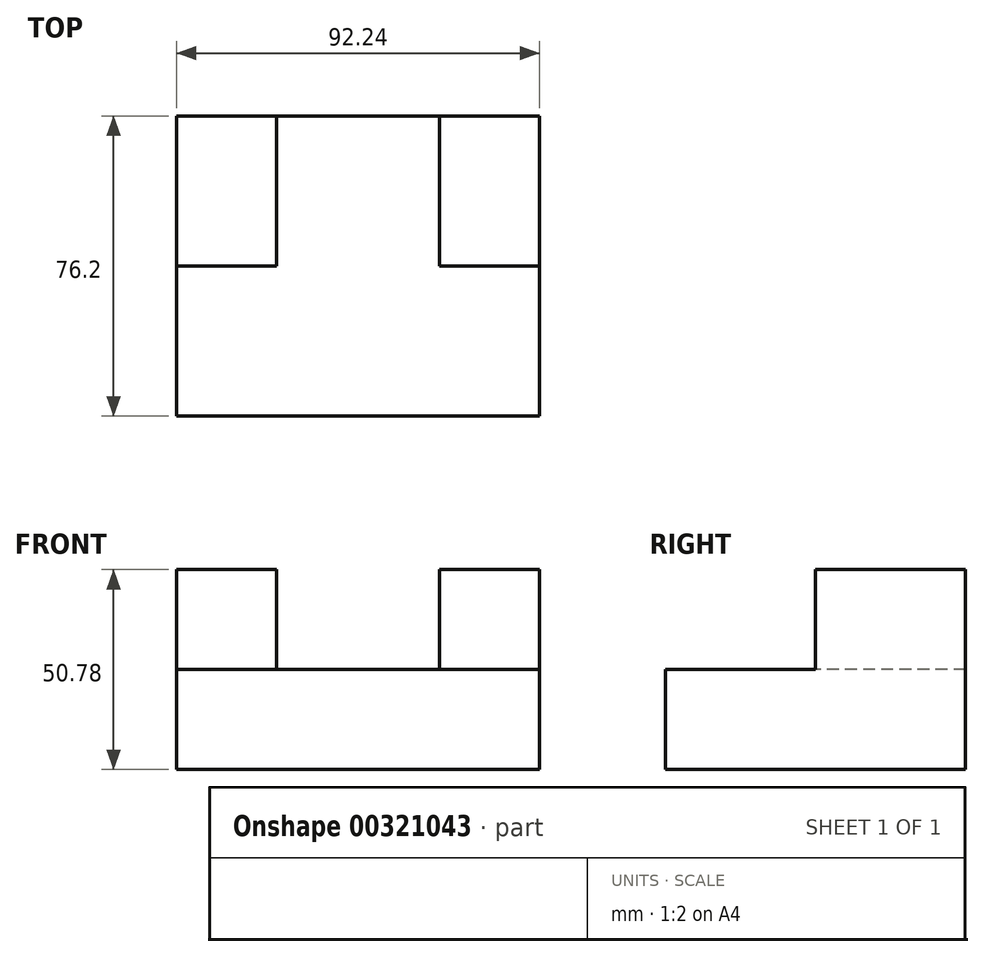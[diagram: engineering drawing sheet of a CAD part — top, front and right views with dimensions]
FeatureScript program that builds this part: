
annotation { "Feature Type Name" : "Feature", "Feature Type Description" : "" }
export const myFeature = defineFeature(function(context is Context, id is Id, definition is map)
    precondition{}
    {
        {
            var Q0;
            Q0=qCreatedBy(makeId("Front.planeOp"),FACE);
            var sketch = newSketch(context, id + "F0", { "sketchPlane" : qUnion([Q0])});
            skLineSegment(sketch, "E0", {"start": v(-58.8, -31.1) * mm, "end": v(33.43, -31.1) * mm});
            skLineSegment(sketch, "E1", {"start": v(33.43, -31.1) * mm, "end": v(33.43, -5.73) * mm});
            skLineSegment(sketch, "E2", {"start": v(33.43, -5.73) * mm, "end": v(-58.8, -5.73) * mm});
            skLineSegment(sketch, "E3", {"start": v(-58.8, -5.73) * mm, "end": v(-58.8, -31.1) * mm});
            skSolve(sketch);
        }
        {
            var Q0;
            Q0=makeQuery(id+"F0.imprint","IMPRINT",FACE,{"disambiguationData":[TD([[makeQuery(id+"F0.imprint","IMPRINT",EDGE,{"derivedFrom":sQuery(id+"F0.wireOp",EDGE,"E0")}),1.0]])]});
            extrude(context, id + "F1", {"entities" : qUnion([Q0]), "depth" : 76.2 * mm});
        }
        {
            var Q0;
            Q0=makeQuery(id+"F1.opExtrude","SWEPT_FACE",FACE,{"disambiguationData":[OSD([sQuery(id+"F0.wireOp",EDGE,"E2")])]});
            var sketch = newSketch(context, id + "F2", { "sketchPlane" : qUnion([Q0])});
            skLineSegment(sketch, "E4", {"start": v(-33.4, 0) * mm, "end": v(-33.4, -38.1) * mm});
            skLineSegment(sketch, "E5", {"start": v(-33.4, -38.1) * mm, "end": v(-58.8, -38.1) * mm});
            skLineSegment(sketch, "E6", {"start": v(-58.8, -38.1) * mm, "end": v(-58.8, 0) * mm});
            skLineSegment(sketch, "E7", {"start": v(-58.8, 0) * mm, "end": v(-33.4, 0) * mm});
            skSolve(sketch);
        }
        {
            var Q0;
            Q0=makeQuery(id+"F2.imprint","IMPRINT",FACE,{"disambiguationData":[TD([[makeQuery(id+"F2.imprint","IMPRINT",EDGE,{"derivedFrom":sQuery(id+"F2.wireOp",EDGE,"E4")}),-1.0]])]});
            extrude(context, id + "F3", {"entities" : qUnion([Q0]), "operationType" : NewBodyOperationType.ADD, "depth" : 25.4 * mm});
        }
        {
            var Q0;
            Q0=makeQuery(id+"F1.opExtrude","SWEPT_FACE",FACE,{"disambiguationData":[OSD([sQuery(id+"F0.wireOp",EDGE,"E2")])]});
            var sketch = newSketch(context, id + "F4", { "sketchPlane" : qUnion([Q0])});
            skLineSegment(sketch, "E8", {"start": v(8.03, 0) * mm, "end": v(8.03, -38.1) * mm});
            skLineSegment(sketch, "E9", {"start": v(8.03, -38.1) * mm, "end": v(33.43, -38.1) * mm});
            skLineSegment(sketch, "E10", {"start": v(33.43, -38.1) * mm, "end": v(33.43, 0) * mm});
            skLineSegment(sketch, "E11", {"start": v(33.43, 0) * mm, "end": v(8.03, 0) * mm});
            skSolve(sketch);
        }
        {
            var Q0;
            Q0=makeQuery(id+"F4.imprint","IMPRINT",FACE,{"disambiguationData":[TD([[makeQuery(id+"F4.imprint","IMPRINT",EDGE,{"derivedFrom":sQuery(id+"F4.wireOp",EDGE,"E8")}),1.0]])]});
            extrude(context, id + "F5", {"entities" : qUnion([Q0]), "operationType" : NewBodyOperationType.ADD, "depth" : 25.4 * mm});
        }
    });
